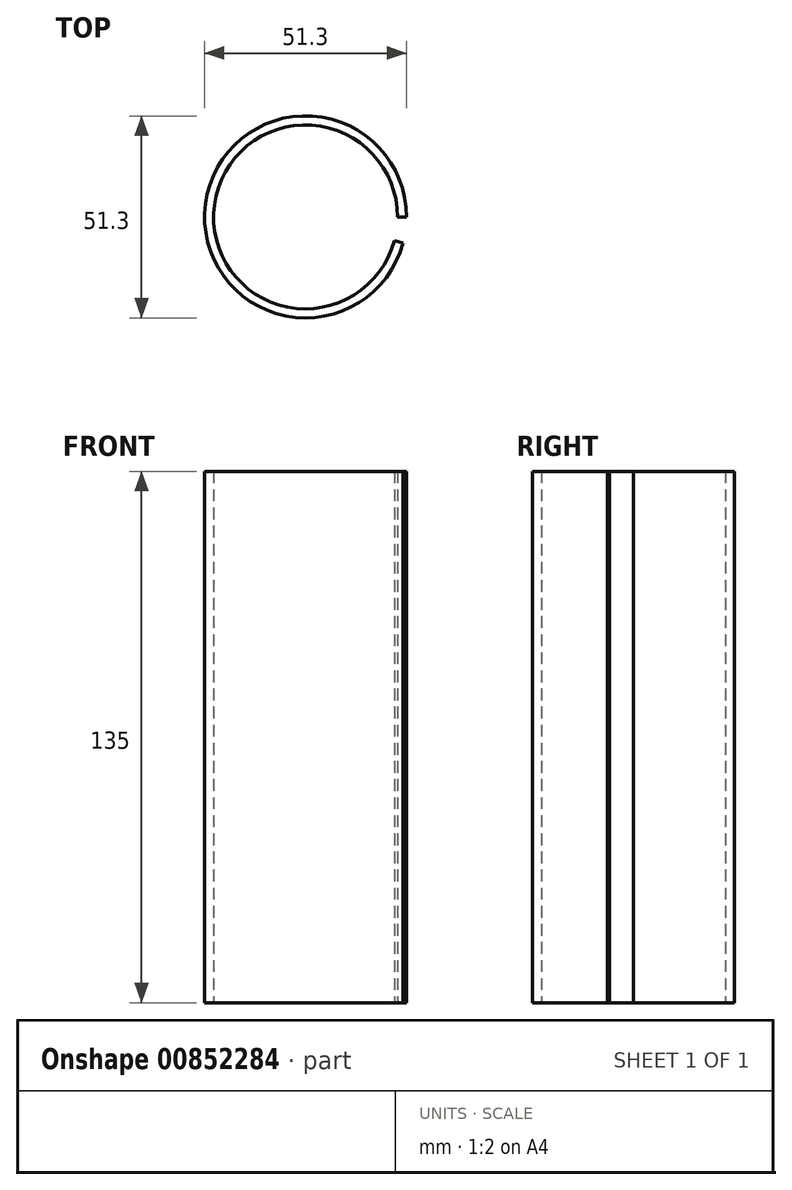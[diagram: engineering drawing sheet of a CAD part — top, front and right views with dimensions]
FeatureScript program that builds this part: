
annotation { "Feature Type Name" : "Feature", "Feature Type Description" : "" }
export const myFeature = defineFeature(function(context is Context, id is Id, definition is map)
    precondition{}
    {
        {
            var Q0;
            Q0=qCreatedBy(makeId("Top.planeOp"),FACE);
            var sketch = newSketch(context, id + "F0", { "sketchPlane" : qUnion([Q0])});
            skCircle(sketch, "E0", {"center": v(0, 0) * mm, "radius": 25.65 * mm});
            skCircle(sketch, "E1", {"center": v(0, 0) * mm, "radius": 23.37 * mm});
            skLineSegment(sketch, "E2", {"start": v(0, 0) * mm, "end": v(25.65, 0) * mm});
            skLineSegment(sketch, "E3", {"start": v(0, 0) * mm, "end": v(24.78, -6.64) * mm});
            skSolve(sketch);
        }
        {
            var Q0;
            {var subQ0=sQuery(id+"F0.wireOp",EDGE,"E2");var subQ1=sQuery(id+"F0.wireOp",EDGE,"E0");var subQ2=makeQuery(id+"F0.imprint","INTERSECT",VERTEX,{"derivedFrom":[subQ1,subQ0]});Q0=makeQuery(id+"F0.imprint","IMPRINT",FACE,{"disambiguationData":[TD([[makeQuery(id+"F0.imprint","IMPRINT",EDGE,{"disambiguationData":[TD([[subQ2,-1.0]])],"derivedFrom":subQ1}),1.0]])]});}
            extrude(context, id + "F1", {"entities" : qUnion([Q0]), "depth" : 135 * mm, "offsetDistance" : 25.4 * mm});
        }
    });
